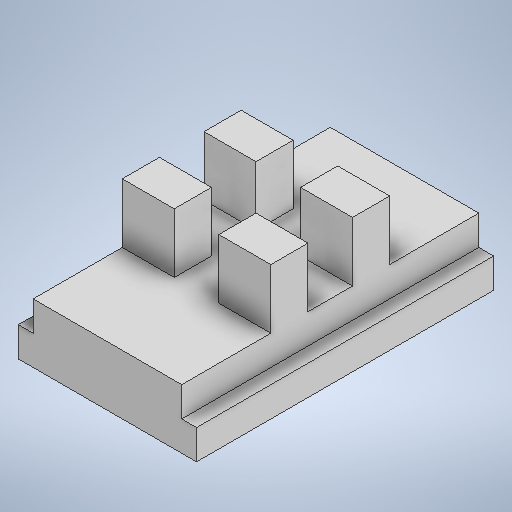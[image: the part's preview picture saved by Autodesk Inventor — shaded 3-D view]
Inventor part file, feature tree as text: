
AUTODESK INVENTOR PART (.ipt)
format: ipt  version: 2025.1 (Build 291241000, 241)  size: 278,016 bytes
history: native  units: mm
features: extrude x4, sketch x4, mirror x1
ambient origin geometry x8: Origin, YZ Plane, XZ Plane, XY Plane, X Axis, Y Axis, Z Axis, Center Point
bodies: Solid1 (feature_tree)
feature tree (9):
  extrude  "Extrusion1"  Depth=20.0mm
  extrude  "Extrusion2"  Depth=10.0mm
  extrude  "Extrusion3"  Depth=6.0mm
  mirror  "Mirror1"
  extrude  "Extrusion4"  Depth=6.0mm
  sketch  "Sketch1"  dims[d0=12.0mm d1=20.0mm]
  sketch  "Sketch2"  dims[d2=2.0mm d3=0.0mm d4=10.0mm]
  sketch  "Sketch3"  dims[d5=2.0mm d6=0.0mm d7=6.0mm]
  sketch  "Sketch4"  dims[d8=2.5mm d9=6.0mm d10=2.5mm d11=1.5mm d12=4.0mm d13=0.0mm d14=12.5mm d15=3.75mm d16=7.0mm d17=3.0mm d18=0.0mm]
